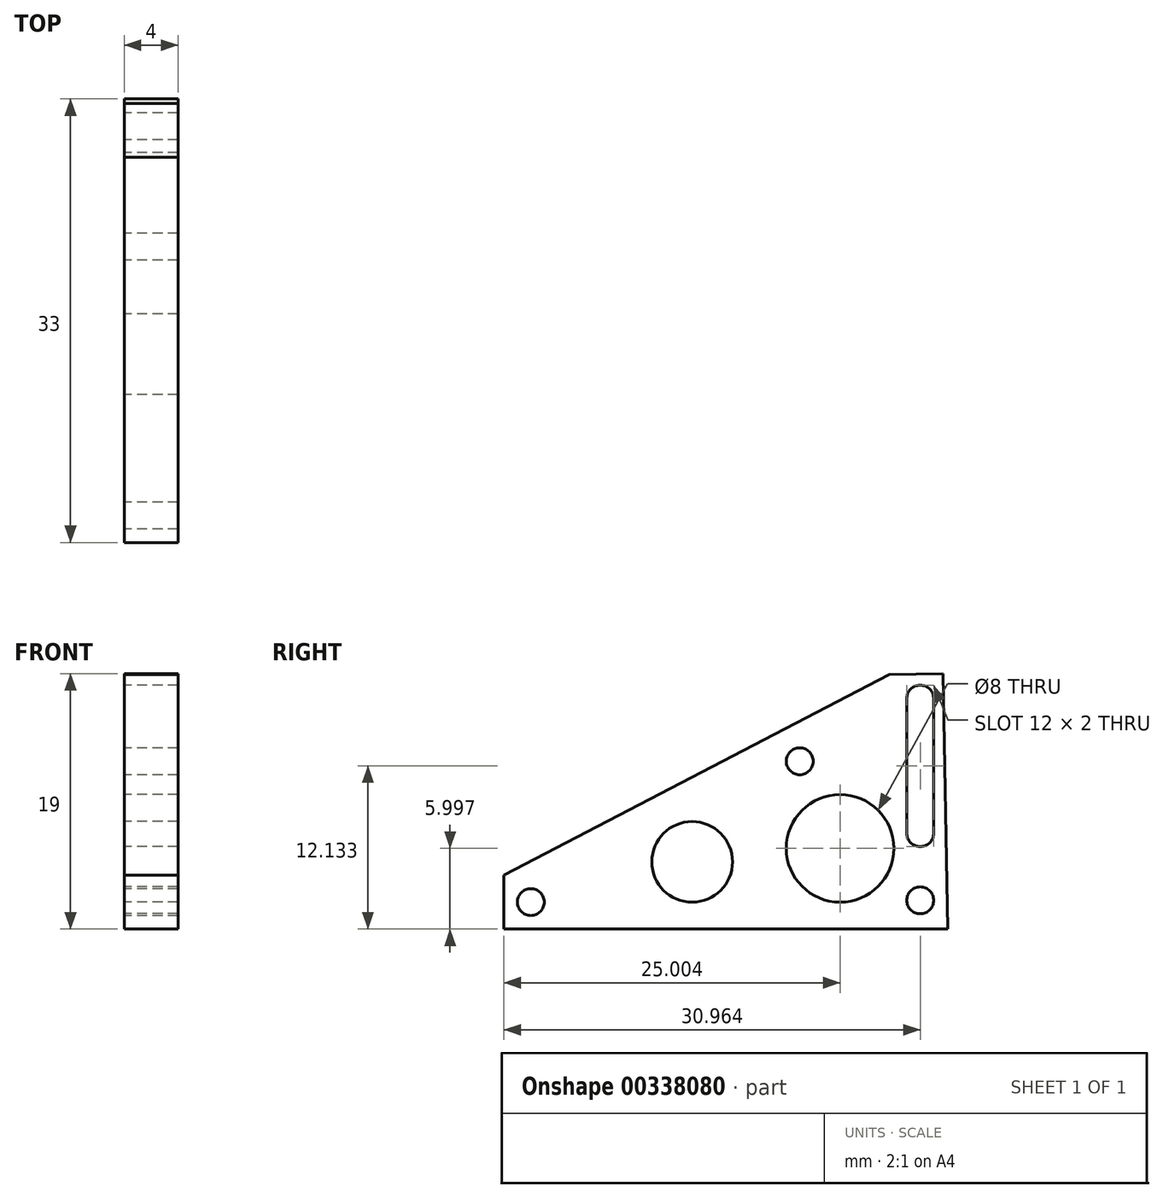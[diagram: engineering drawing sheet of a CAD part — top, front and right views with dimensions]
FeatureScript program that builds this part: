
annotation { "Feature Type Name" : "Feature", "Feature Type Description" : "" }
export const myFeature = defineFeature(function(context is Context, id is Id, definition is map)
    precondition{}
    {
        {
            var Q0;
            Q0=qCreatedBy(makeId("Right.planeOp"),FACE);
            var sketch = newSketch(context, id + "F0", { "sketchPlane" : qUnion([Q0])});
            skLineSegment(sketch, "E0", {"start": v(36.88, 9.44) * mm, "end": v(37.22, -9.56) * mm});
            skLineSegment(sketch, "E1", {"start": v(37.22, -9.56) * mm, "end": v(4.22, -9.56) * mm});
            skLineSegment(sketch, "E2", {"start": v(36.88, 9.44) * mm, "end": v(32.88, 9.36) * mm});
            skLineSegment(sketch, "E3", {"start": v(4.22, -9.56) * mm, "end": v(4.22, -5.56) * mm});
            skLineSegment(sketch, "E4", {"start": v(4.22, -5.56) * mm, "end": v(32.88, 9.36) * mm});
            skCircle(sketch, "E5", {"center": v(29.22, -3.56) * mm, "radius": 4 * mm});
            skCircle(sketch, "E6", {"center": v(18.22, -4.56) * mm, "radius": 3 * mm});
            skCircle(sketch, "E7", {"center": v(26.22, 2.92) * mm, "radius": 1 * mm});
            skCircle(sketch, "E8", {"center": v(6.22, -7.56) * mm, "radius": 1 * mm});
            skCircle(sketch, "E9", {"center": v(35.18, -7.43) * mm, "radius": 1 * mm});
            skLineSegment(sketch, "E10.bottom", {"start": v(34.18, 7.57) * mm, "end": v(36.18, 7.57) * mm});
            skLineSegment(sketch, "E10.top", {"start": v(34.18, -2.43) * mm, "end": v(36.18, -2.43) * mm});
            skLineSegment(sketch, "E10.left", {"start": v(34.18, 7.57) * mm, "end": v(34.18, -2.43) * mm});
            skLineSegment(sketch, "E10.right", {"start": v(36.18, 7.57) * mm, "end": v(36.18, -2.43) * mm});
            skArc(sketch, "E11", {"start": v(34.18, -2.43) * mm, "mid": v(35.18, -3.43) * mm, "end": v(36.18, -2.43) * mm});
            skArc(sketch, "E12", {"start": v(36.18, 7.57) * mm, "mid": v(35.18, 8.57) * mm, "end": v(34.18, 7.57) * mm});
            skSolve(sketch);
        }
        {
            var Q0;
            Q0=makeQuery(id+"F0.imprint","IMPRINT",FACE,{"disambiguationData":[TD([[makeQuery(id+"F0.imprint","IMPRINT",EDGE,{"derivedFrom":sQuery(id+"F0.wireOp",EDGE,"E0")}),-1.0]])]});
            extrude(context, id + "F1", {"entities" : qUnion([Q0]), "endBound" : BoundingType.SYMMETRIC, "depth" : 4 * mm});
        }
    });
